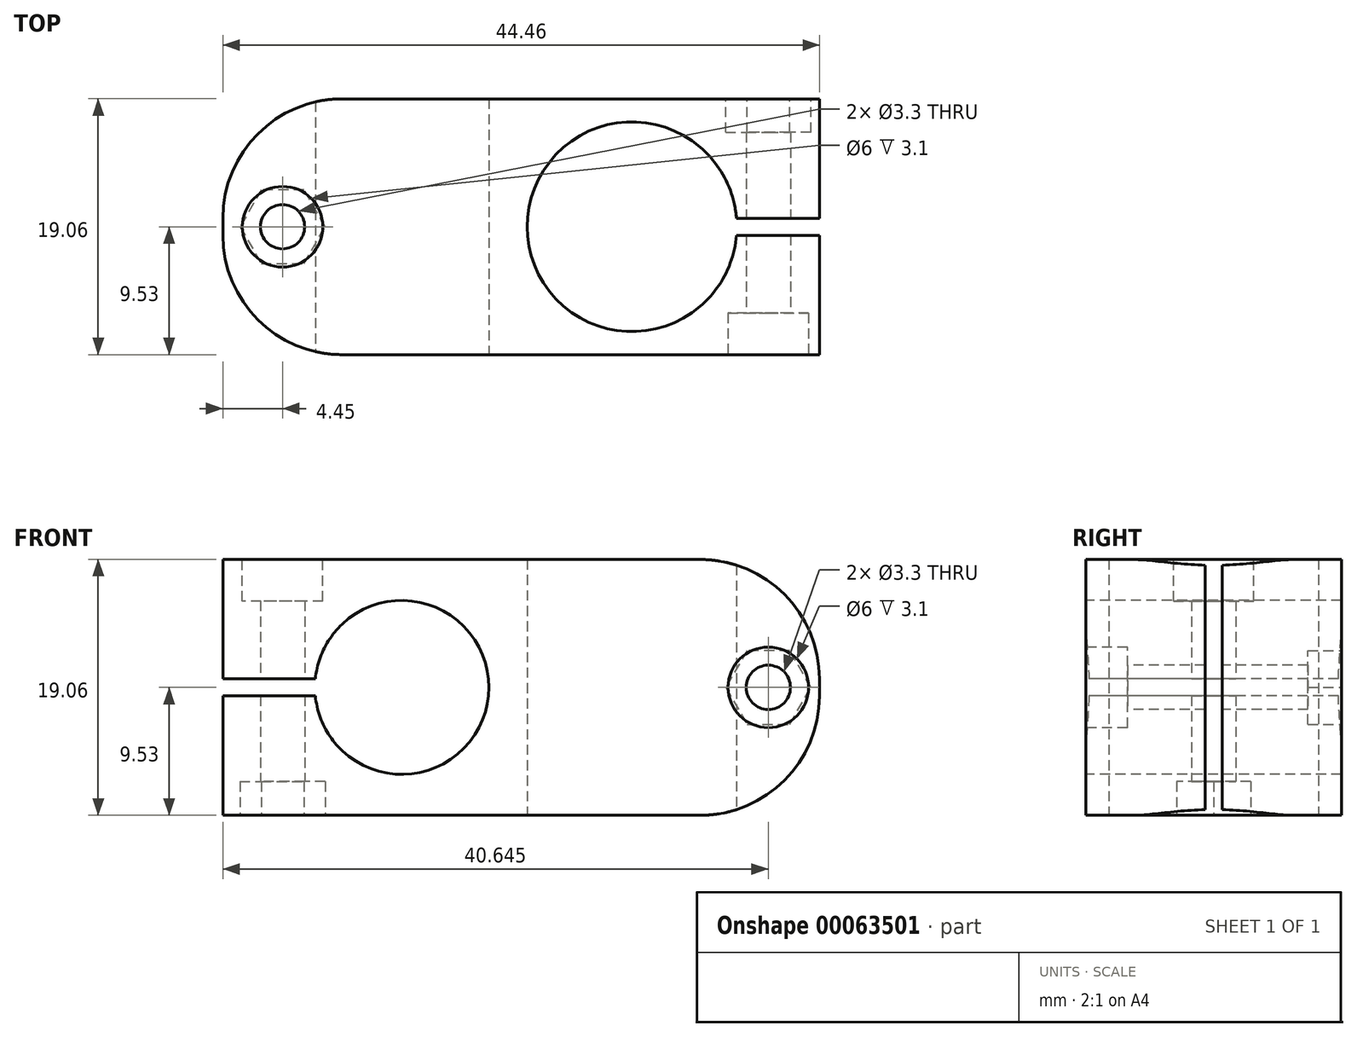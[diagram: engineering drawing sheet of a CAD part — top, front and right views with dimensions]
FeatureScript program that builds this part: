
annotation { "Feature Type Name" : "Feature", "Feature Type Description" : "" }
export const myFeature = defineFeature(function(context is Context, id is Id, definition is map)
    precondition{}
    {
        {
            var Q0;
            Q0=qCreatedBy(makeId("Top.planeOp"),FACE);
            var sketch = newSketch(context, id + "F0", { "sketchPlane" : qUnion([Q0])});
            skLineSegment(sketch, "E0.bottom", {"start": v(-22.22, 9.53) * mm, "end": v(22.22, 9.52) * mm});
            skLineSegment(sketch, "E0.top", {"start": v(-22.22, -9.52) * mm, "end": v(22.22, -9.53) * mm});
            skLineSegment(sketch, "E0.left", {"start": v(-22.22, 9.53) * mm, "end": v(-22.23, -9.53) * mm});
            skLineSegment(sketch, "E0.right", {"start": v(22.22, 9.53) * mm, "end": v(22.22, -9.53) * mm});
            skCircle(sketch, "E1", {"center": v(8.26, 0) * mm, "radius": 7.81 * mm});
            skLineSegment(sketch, "E2.bottom", {"start": v(8.26, 0.64) * mm, "end": v(22.22, 0.64) * mm});
            skLineSegment(sketch, "E2.top", {"start": v(8.26, -0.64) * mm, "end": v(22.22, -0.64) * mm});
            skLineSegment(sketch, "E2.left", {"start": v(8.26, 0.64) * mm, "end": v(8.26, -0.64) * mm});
            skLineSegment(sketch, "E2.right", {"start": v(22.22, 0.64) * mm, "end": v(22.22, -0.64) * mm});
            skCircle(sketch, "E3", {"center": v(-17.78, 0) * mm, "radius": 1.65 * mm});
            skSolve(sketch);
        }
        {
            var Q0;
            {var subQ1=sQuery(id+"F0.wireOp",EDGE,"E0.bottom");Q0=makeQuery(id+"F0.imprint","IMPRINT",FACE,{"disambiguationData":[TD([[makeQuery(id+"F0.imprint","IMPRINT",EDGE,{"derivedFrom":subQ1}),-1.0]])]});}
            extrude(context, id + "F1", {"entities" : qUnion([Q0]), "endBound" : BoundingType.SYMMETRIC, "depth" : 19.05 * mm});
        }
        {
            var Q0;
            Q0=qCreatedBy(makeId("Front.planeOp"),FACE);
            var sketch = newSketch(context, id + "F2", { "sketchPlane" : qUnion([Q0])});
            skCircle(sketch, "E4", {"center": v(-8.9, 0) * mm, "radius": 6.48 * mm});
            skLineSegment(sketch, "E5.0.0", {"start": v(-22.23, -9.53) * mm, "end": v(22.22, -9.53) * mm, "construction": true});
            skLineSegment(sketch, "E5.0.1", {"start": v(22.22, -9.53) * mm, "end": v(22.22, 9.53) * mm, "construction": true});
            skLineSegment(sketch, "E5.0.2", {"start": v(22.22, 9.53) * mm, "end": v(-22.23, 9.53) * mm, "construction": true});
            skLineSegment(sketch, "E5.0.3", {"start": v(-22.23, 9.53) * mm, "end": v(-22.23, -9.53) * mm, "construction": true});
            skLineSegment(sketch, "E6.bottom", {"start": v(-8.9, 0.63) * mm, "end": v(-22.23, 0.63) * mm});
            skLineSegment(sketch, "E6.top", {"start": v(-8.9, -0.63) * mm, "end": v(-22.23, -0.63) * mm});
            skLineSegment(sketch, "E6.left", {"start": v(-8.9, 0.63) * mm, "end": v(-8.9, -0.63) * mm});
            skLineSegment(sketch, "E6.right", {"start": v(-22.23, 0.64) * mm, "end": v(-22.23, -0.64) * mm});
            skCircle(sketch, "E7", {"center": v(18.41, 0) * mm, "radius": 1.65 * mm});
            skSolve(sketch);
        }
        {
            var Q0;
            {var subQ5=sQuery(id+"F2.wireOp",EDGE,"E6.right");Q0=makeQuery(id+"F2.imprint","IMPRINT",FACE,{"disambiguationData":[TD([[makeQuery(id+"F2.imprint","IMPRINT",EDGE,{"derivedFrom":subQ5}),1.0]])]});}
            var Q1;
            {var subQ5=sQuery(id+"F2.wireOp",EDGE,"E6.left");Q1=makeQuery(id+"F2.imprint","IMPRINT",FACE,{"disambiguationData":[TD([[makeQuery(id+"F2.imprint","IMPRINT",EDGE,{"derivedFrom":subQ5}),-1.0]])]});}
            var Q2;
            {var subQ5=sQuery(id+"F2.wireOp",EDGE,"E6.left");Q2=makeQuery(id+"F2.imprint","IMPRINT",FACE,{"disambiguationData":[TD([[makeQuery(id+"F2.imprint","IMPRINT",EDGE,{"derivedFrom":subQ5}),1.0]])]});}
            var Q3;
            Q3=makeQuery(id+"F2.imprint","IMPRINT",FACE,{"disambiguationData":[TD([[makeQuery(id+"F2.imprint","IMPRINT",EDGE,{"derivedFrom":sQuery(id+"F2.wireOp",EDGE,"E7")}),1.0]])]});
            extrude(context, id + "F3", {"entities" : qUnion([Q0, Q1, Q2, Q3]), "operationType" : NewBodyOperationType.REMOVE, "endBound" : BoundingType.SYMMETRIC, "oppositeDirection" : true, "depth" : 50.8 * mm});
        }
        {
            var Q0;
            Q0=makeQuery(id+"F1.opExtrude","SWEPT_FACE",FACE,{"disambiguationData":[OSD([sQuery(id+"F0.wireOp",EDGE,"E0.top")])]});
            var sketch = newSketch(context, id + "F4", { "sketchPlane" : qUnion([Q0])});
            skCircle(sketch, "E8", {"center": v(18.41, 0) * mm, "radius": 3 * mm});
            skSolve(sketch);
        }
        {
            var Q0;
            Q0=makeQuery(id+"F4.imprint","IMPRINT",FACE,{"disambiguationData":[TD([[makeQuery(id+"F4.imprint","IMPRINT",EDGE,{"derivedFrom":sQuery(id+"F4.wireOp",EDGE,"E8")}),1.0]])]});
            extrude(context, id + "F5", {"entities" : qUnion([Q0]), "operationType" : NewBodyOperationType.REMOVE, "oppositeDirection" : true, "depth" : 3.1 * mm});
        }
        {
            var Q0;
            Q0=makeQuery(id+"F1.opExtrude","CAP_FACE",FACE,{"disambiguationData":[OSD([sQuery(id+"F0.wireOp",EDGE,"E0.bottom"),sQuery(id+"F0.wireOp",EDGE,"E0.top"),sQuery(id+"F0.wireOp",EDGE,"E0.left"),sQuery(id+"F0.wireOp",EDGE,"E0.right"),sQuery(id+"F0.wireOp",EDGE,"E1"),sQuery(id+"F0.wireOp",EDGE,"E2.bottom"),sQuery(id+"F0.wireOp",EDGE,"E2.top"),sQuery(id+"F0.wireOp",EDGE,"E3")])],"isStart":false});
            var sketch = newSketch(context, id + "F6", { "sketchPlane" : qUnion([Q0])});
            skCircle(sketch, "E9", {"center": v(-17.78, 0) * mm, "radius": 3 * mm});
            skSolve(sketch);
        }
        {
            var Q0;
            Q0=makeQuery(id+"F6.imprint","IMPRINT",FACE,{"disambiguationData":[TD([[makeQuery(id+"F6.imprint","IMPRINT",EDGE,{"derivedFrom":sQuery(id+"F6.wireOp",EDGE,"E9")}),1.0]])]});
            extrude(context, id + "F7", {"entities" : qUnion([Q0]), "operationType" : NewBodyOperationType.REMOVE, "oppositeDirection" : true, "depth" : 3.1 * mm});
        }
        {
            var Q0;
            Q0=makeQuery(id+"F1.opExtrude","SWEPT_FACE",FACE,{"disambiguationData":[OSD([sQuery(id+"F0.wireOp",EDGE,"E0.bottom")])]});
            var sketch = newSketch(context, id + "F8", { "sketchPlane" : qUnion([Q0])});
            skCircle(sketch, "E10.cCircle", {"center": v(-18.41, 0) * mm, "radius": 2.75 * mm, "construction": true});
            skLineSegment(sketch, "E10.0", {"start": v(-20, 2.75) * mm, "end": v(-16.83, 2.75) * mm});
            skLineSegment(sketch, "E10.1", {"start": v(-16.83, 2.75) * mm, "end": v(-15.24, 0) * mm});
            skLineSegment(sketch, "E10.2", {"start": v(-15.24, 0) * mm, "end": v(-16.83, -2.75) * mm});
            skLineSegment(sketch, "E10.3", {"start": v(-16.83, -2.75) * mm, "end": v(-20, -2.75) * mm});
            skLineSegment(sketch, "E10.4", {"start": v(-20, -2.75) * mm, "end": v(-21.6, 0) * mm});
            skLineSegment(sketch, "E10.5", {"start": v(-21.6, 0) * mm, "end": v(-20, 2.75) * mm});
            skPoint(sketch, "E10.0.midPoint", {"position": v(-18.41, 2.75) * mm});
            skSolve(sketch);
        }
        {
            var Q0;
            Q0=makeQuery(id+"F8.imprint","IMPRINT",FACE,{"disambiguationData":[TD([[makeQuery(id+"F8.imprint","IMPRINT",EDGE,{"derivedFrom":sQuery(id+"F8.wireOp",EDGE,"E10.0")}),-1.0]])]});
            extrude(context, id + "F9", {"entities" : qUnion([Q0]), "operationType" : NewBodyOperationType.REMOVE, "oppositeDirection" : true, "depth" : 2.5 * mm});
        }
        {
            var Q0;
            Q0=makeQuery(id+"F1.opExtrude","CAP_FACE",FACE,{"disambiguationData":[OSD([sQuery(id+"F0.wireOp",EDGE,"E0.bottom"),sQuery(id+"F0.wireOp",EDGE,"E0.top"),sQuery(id+"F0.wireOp",EDGE,"E0.left"),sQuery(id+"F0.wireOp",EDGE,"E0.right"),sQuery(id+"F0.wireOp",EDGE,"E1"),sQuery(id+"F0.wireOp",EDGE,"E2.bottom"),sQuery(id+"F0.wireOp",EDGE,"E2.top"),sQuery(id+"F0.wireOp",EDGE,"E3")])],"isStart":true});
            var sketch = newSketch(context, id + "F10", { "sketchPlane" : qUnion([Q0])});
            skCircle(sketch, "E11.cCircle", {"center": v(-17.78, 0) * mm, "radius": 2.75 * mm, "construction": true});
            skLineSegment(sketch, "E11.0", {"start": v(-19.37, 2.75) * mm, "end": v(-16.2, 2.75) * mm});
            skLineSegment(sketch, "E11.1", {"start": v(-16.2, 2.75) * mm, "end": v(-14.6, 0) * mm});
            skLineSegment(sketch, "E11.2", {"start": v(-14.6, 0) * mm, "end": v(-16.2, -2.75) * mm});
            skLineSegment(sketch, "E11.3", {"start": v(-16.2, -2.75) * mm, "end": v(-19.37, -2.75) * mm});
            skLineSegment(sketch, "E11.4", {"start": v(-19.37, -2.75) * mm, "end": v(-20.96, 0) * mm});
            skLineSegment(sketch, "E11.5", {"start": v(-20.96, 0) * mm, "end": v(-19.37, 2.75) * mm});
            skPoint(sketch, "E11.0.midPoint", {"position": v(-17.78, 2.75) * mm});
            skSolve(sketch);
        }
        {
            var Q0;
            Q0=makeQuery(id+"F10.imprint","IMPRINT",FACE,{"disambiguationData":[TD([[makeQuery(id+"F10.imprint","IMPRINT",EDGE,{"derivedFrom":sQuery(id+"F10.wireOp",EDGE,"E11.0")}),-1.0]])]});
            extrude(context, id + "F11", {"entities" : qUnion([Q0]), "operationType" : NewBodyOperationType.REMOVE, "oppositeDirection" : true, "depth" : 2.5 * mm});
        }
        {
            var Q0;
            {var subQ0=sQuery(id+"F0.wireOp",EDGE,"E0.right");Q0=makeQuery(id+"F1.opExtrude","CAP_EDGE",EDGE,{"disambiguationData":[OSD([subQ0]),TDD([makeQuery(id+"F0.imprint","IMPRINT",EDGE,{"disambiguationData":[TD([[makeQuery(id+"F0.imprint","INTERSECT",VERTEX,{"derivedFrom":[sQuery(id+"F0.wireOp",EDGE,"E0.top"),subQ0]}),1.0]])],"derivedFrom":subQ0})])],"isStart":false});}
            var Q1;
            {var subQ0=sQuery(id+"F0.wireOp",EDGE,"E0.right");Q1=makeQuery(id+"F1.opExtrude","CAP_EDGE",EDGE,{"disambiguationData":[OSD([subQ0]),TDD([makeQuery(id+"F0.imprint","IMPRINT",EDGE,{"disambiguationData":[TD([[makeQuery(id+"F0.imprint","INTERSECT",VERTEX,{"derivedFrom":[sQuery(id+"F0.wireOp",EDGE,"E0.bottom"),subQ0]}),-1.0]])],"derivedFrom":subQ0})])],"isStart":false});}
            var Q2;
            {var subQ0=sQuery(id+"F0.wireOp",EDGE,"E0.right");Q2=makeQuery(id+"F1.opExtrude","CAP_EDGE",EDGE,{"disambiguationData":[OSD([subQ0]),TDD([makeQuery(id+"F0.imprint","IMPRINT",EDGE,{"disambiguationData":[TD([[makeQuery(id+"F0.imprint","INTERSECT",VERTEX,{"derivedFrom":[sQuery(id+"F0.wireOp",EDGE,"E0.top"),subQ0]}),1.0]])],"derivedFrom":subQ0})])],"isStart":true});}
            var Q3;
            {var subQ0=sQuery(id+"F0.wireOp",EDGE,"E0.right");Q3=makeQuery(id+"F1.opExtrude","CAP_EDGE",EDGE,{"disambiguationData":[OSD([subQ0]),TDD([makeQuery(id+"F0.imprint","IMPRINT",EDGE,{"disambiguationData":[TD([[makeQuery(id+"F0.imprint","INTERSECT",VERTEX,{"derivedFrom":[sQuery(id+"F0.wireOp",EDGE,"E0.bottom"),subQ0]}),-1.0]])],"derivedFrom":subQ0})])],"isStart":true});}
            var Q4;
            {var subQ0=sQuery(id+"F0.wireOp",EDGE,"E0.left");var subQ1=sQuery(id+"F0.wireOp",EDGE,"E0.top");Q4=makeQuery(id+"F3.boolean.opBoolean","SPLIT",EDGE,{"disambiguationData":[TD([makeQuery(id+"F3.opExtrude","SWEPT_FACE",FACE,{"disambiguationData":[OSD([sQuery(id+"F2.wireOp",EDGE,"E6.bottom")])]})])],"derivedFrom":makeQuery(id+"F1.opExtrude","SWEPT_EDGE",EDGE,{"disambiguationData":[OSD([subQ1,subQ0])]})});}
            var Q5;
            {var subQ0=sQuery(id+"F0.wireOp",EDGE,"E0.left");var subQ1=sQuery(id+"F0.wireOp",EDGE,"E0.top");Q5=makeQuery(id+"F3.boolean.opBoolean","SPLIT",EDGE,{"disambiguationData":[TD([makeQuery(id+"F3.opExtrude","SWEPT_FACE",FACE,{"disambiguationData":[OSD([sQuery(id+"F2.wireOp",EDGE,"E6.top")])]})])],"derivedFrom":makeQuery(id+"F1.opExtrude","SWEPT_EDGE",EDGE,{"disambiguationData":[OSD([subQ1,subQ0])]})});}
            var Q6;
            {var subQ0=sQuery(id+"F0.wireOp",EDGE,"E0.bottom");var subQ1=sQuery(id+"F0.wireOp",EDGE,"E0.left");Q6=makeQuery(id+"F3.boolean.opBoolean","SPLIT",EDGE,{"disambiguationData":[TD([makeQuery(id+"F3.opExtrude","SWEPT_FACE",FACE,{"disambiguationData":[OSD([sQuery(id+"F2.wireOp",EDGE,"E6.bottom")])]})])],"derivedFrom":makeQuery(id+"F1.opExtrude","SWEPT_EDGE",EDGE,{"disambiguationData":[OSD([subQ0,subQ1])]})});}
            var Q7;
            {var subQ0=sQuery(id+"F0.wireOp",EDGE,"E0.bottom");var subQ1=sQuery(id+"F0.wireOp",EDGE,"E0.left");Q7=makeQuery(id+"F3.boolean.opBoolean","SPLIT",EDGE,{"disambiguationData":[TD([makeQuery(id+"F3.opExtrude","SWEPT_FACE",FACE,{"disambiguationData":[OSD([sQuery(id+"F2.wireOp",EDGE,"E6.top")])]})])],"derivedFrom":makeQuery(id+"F1.opExtrude","SWEPT_EDGE",EDGE,{"disambiguationData":[OSD([subQ0,subQ1])]})});}
            fillet(context, id + "F12", {"entities" : qUnion([Q0, Q1, Q2, Q3, Q4, Q5, Q6, Q7]), "radius" : 8.9 * mm, "tangentPropagation" : true, "allowEdgeOverflow" : false});
        }
    });
